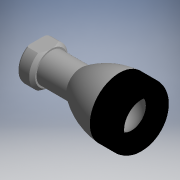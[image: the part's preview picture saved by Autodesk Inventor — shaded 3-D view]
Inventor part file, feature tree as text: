
AUTODESK INVENTOR PART (.ipt)
format: ipt  version: 2017.3 (Build 213256000, 256)  size: 190,976 bytes
history: native  units: mm (DEFAULTED — no unit token found)
features: other x7, sketch x4, revolve x2, extrude x1, hole x1
ambient origin geometry x8: Origin, YZ Plane, XZ Plane, XY Plane, X Axis, Y Axis, Z Axis, Center Point
bodies: Solid1 (feature_tree)
feature tree (15):
  revolve  "Revolution1"  [1 undecoded]
  extrude  "Extrusion1"  [1 undecoded]
  revolve  "Revolution2"  [1 undecoded]
  hole  "Hole1"  [1 undecoded]
  other  "holder_XY"
  other  "holder_YZ"
  other  "holder_ZX"
  other  "holder_X"
  other  "holder_Y"
  other  "holder_Z"
  other  "holder_Center"
  sketch  "Sketch_1"  dims[d0=360.0deg d1=5.0mm d2=0.0mm]
  sketch  "Sketch_2"  dims[d3=360.0deg]
  sketch  "Sketch_6"
  sketch  "Sketch4"  dims[d4=4.917mm d5=15.5415mm d6=6.0mm d7=2.0mm d8=90.0deg d9=16.580584mm d10=120.0deg]
note: 4 required parameter values undecoded (feature->parameter linkage not recoverable at this tier; creation-order binding heuristic only, values carry confidence <= 0.55)